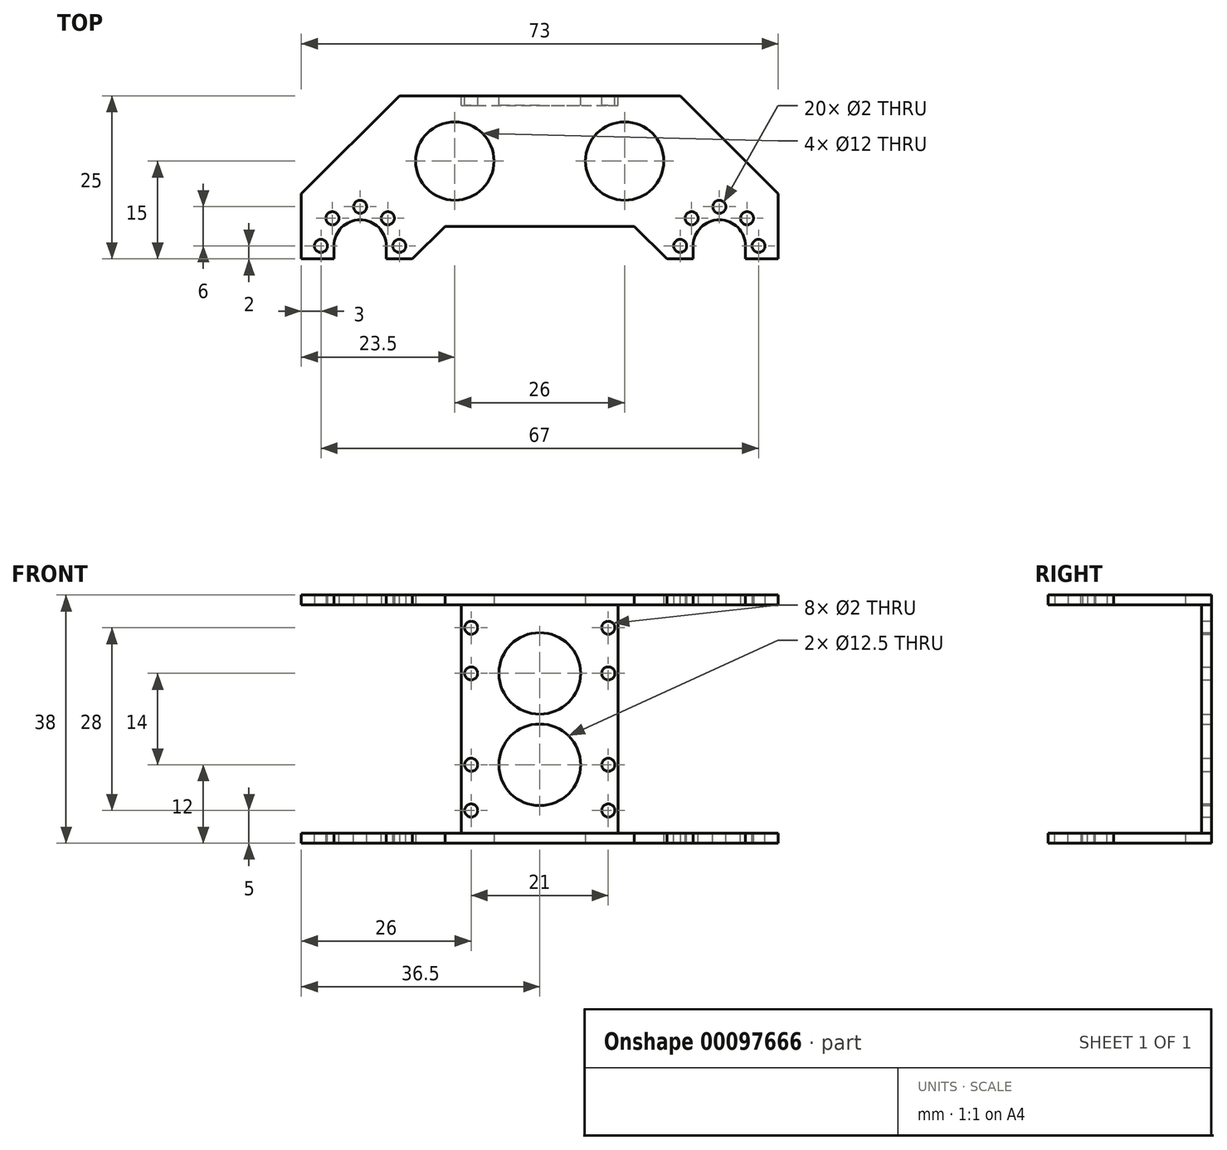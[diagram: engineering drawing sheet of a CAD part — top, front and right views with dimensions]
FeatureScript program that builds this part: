
annotation { "Feature Type Name" : "Feature", "Feature Type Description" : "" }
export const myFeature = defineFeature(function(context is Context, id is Id, definition is map)
    precondition{}
    {
        {
            var Q0;
            Q0=qCreatedBy(makeId("Top.planeOp"),FACE);
            var sketch = newSketch(context, id + "F0", { "sketchPlane" : qUnion([Q0])});
            skLineSegment(sketch, "E0.bottom", {"start": v(-36.5, 0) * mm, "end": v(-31.5, 0) * mm});
            skLineSegment(sketch, "E0.top", {"start": v(-36.5, 25) * mm, "end": v(36.5, 25) * mm});
            skLineSegment(sketch, "E0.left", {"start": v(-36.5, 0) * mm, "end": v(-36.5, 25) * mm});
            skLineSegment(sketch, "E0.right", {"start": v(36.5, 0) * mm, "end": v(36.5, 25) * mm});
            skLineSegment(sketch, "E1", {"start": v(0, 25) * mm, "end": v(0, 0) * mm, "construction": true});
            skArc(sketch, "E2", {"start": v(-23.5, 2) * mm, "mid": v(-27.5, 6) * mm, "end": v(-31.5, 2) * mm});
            skCircle(sketch, "E3", {"center": v(-27.5, 8) * mm, "radius": 1 * mm});
            skCircle(sketch, "E4.1.0", {"center": v(-31.74, 6.24) * mm, "radius": 1 * mm});
            skCircle(sketch, "E4.2.0", {"center": v(-33.5, 2) * mm, "radius": 1 * mm});
            skCircle(sketch, "E4.6.0", {"center": v(-21.5, 2) * mm, "radius": 1 * mm});
            skCircle(sketch, "E4.7.0", {"center": v(-23.26, 6.24) * mm, "radius": 1 * mm});
            skLineSegment(sketch, "E5", {"start": v(-23.5, 2) * mm, "end": v(-23.5, 0) * mm});
            skLineSegment(sketch, "E6", {"start": v(-31.5, 2) * mm, "end": v(-31.5, 0) * mm});
            skLineSegment(sketch, "E7.trimOffspring", {"start": v(-23.5, 0) * mm, "end": v(23.5, 0) * mm});
            skCircle(sketch, "E8.MirrorC", {"center": v(33.5, 2) * mm, "radius": 1 * mm});
            skCircle(sketch, "E9.MirrorC", {"center": v(31.74, 6.24) * mm, "radius": 1 * mm});
            skCircle(sketch, "E10.MirrorC", {"center": v(27.5, 8) * mm, "radius": 1 * mm});
            skCircle(sketch, "E11.MirrorC", {"center": v(23.26, 6.24) * mm, "radius": 1 * mm});
            skCircle(sketch, "E12.MirrorC", {"center": v(21.5, 2) * mm, "radius": 1 * mm});
            skArc(sketch, "E13.MirrorCS", {"start": v(23.5, 2) * mm, "mid": v(27.5, 6) * mm, "end": v(31.5, 2) * mm});
            skLineSegment(sketch, "E14.MirrorCS", {"start": v(23.5, 2) * mm, "end": v(23.5, 0) * mm});
            skLineSegment(sketch, "E15.MirrorCS", {"start": v(31.5, 2) * mm, "end": v(31.5, 0) * mm});
            skLineSegment(sketch, "E16.trimOffspring", {"start": v(31.5, 0) * mm, "end": v(36.5, 0) * mm});
            skSolve(sketch);
        }
        {
            var Q0;
            Q0 = qSketchRegion(id + "F0", true);
            extrude(context, id + "F1", {"entities" : qUnion([Q0]), "depth" : 1.5 * mm});
        }
        {
            var Q0;
            Q0=makeQuery(id+"F1.opExtrude","CAP_FACE",FACE,{"disambiguationData":[OSD([sQuery(id+"F0.wireOp",EDGE,"E0.bottom"),sQuery(id+"F0.wireOp",EDGE,"E0.top"),sQuery(id+"F0.wireOp",EDGE,"E0.left"),sQuery(id+"F0.wireOp",EDGE,"E0.right"),sQuery(id+"F0.wireOp",EDGE,"E2"),sQuery(id+"F0.wireOp",EDGE,"E3"),sQuery(id+"F0.wireOp",EDGE,"E4.1.0"),sQuery(id+"F0.wireOp",EDGE,"E4.2.0"),sQuery(id+"F0.wireOp",EDGE,"E4.6.0"),sQuery(id+"F0.wireOp",EDGE,"E4.7.0"),sQuery(id+"F0.wireOp",EDGE,"E5"),sQuery(id+"F0.wireOp",EDGE,"E6"),sQuery(id+"F0.wireOp",EDGE,"E7.trimOffspring"),sQuery(id+"F0.wireOp",EDGE,"E8.MirrorC"),sQuery(id+"F0.wireOp",EDGE,"E9.MirrorC"),sQuery(id+"F0.wireOp",EDGE,"E10.MirrorC"),sQuery(id+"F0.wireOp",EDGE,"E11.MirrorC"),sQuery(id+"F0.wireOp",EDGE,"E12.MirrorC"),sQuery(id+"F0.wireOp",EDGE,"E13.MirrorCS"),sQuery(id+"F0.wireOp",EDGE,"E14.MirrorCS"),sQuery(id+"F0.wireOp",EDGE,"E15.MirrorCS"),sQuery(id+"F0.wireOp",EDGE,"E16.trimOffspring")])],"isStart":false});
            var sketch = newSketch(context, id + "F2", { "sketchPlane" : qUnion([Q0])});
            skLineSegment(sketch, "E17", {"start": v(-36.5, 10) * mm, "end": v(-21.5, 25) * mm});
            skPoint(sketch, "E18", {"position": v(-27.5, 8) * mm});
            skPoint(sketch, "E19", {"position": v(-21.5, 2) * mm});
            skLineSegment(sketch, "E20", {"start": v(-19.5, 0) * mm, "end": v(-14.5, 5) * mm});
            skLineSegment(sketch, "E21", {"start": v(-14.5, 5) * mm, "end": v(0, 5) * mm});
            skLineSegment(sketch, "E22.MirrorCS", {"start": v(19.5, 0) * mm, "end": v(14.5, 5) * mm});
            skLineSegment(sketch, "E23.MirrorCS", {"start": v(14.5, 5) * mm, "end": v(0, 5) * mm});
            skLineSegment(sketch, "E24.MirrorCS", {"start": v(36.5, 10) * mm, "end": v(21.5, 25) * mm});
            skSolve(sketch);
        }
        {
            var Q0;
            {var subQ0=sQuery(id+"F2.wireOp",EDGE,"E17");Q0=makeQuery(id+"F2.imprint","IMPRINT",FACE,{"disambiguationData":[TD([[makeQuery(id+"F2.imprint","IMPRINT",EDGE,{"derivedFrom":subQ0}),1.0]])]});}
            var Q1;
            {var subQ0=sQuery(id+"F2.wireOp",EDGE,"E24.MirrorCS");Q1=makeQuery(id+"F2.imprint","IMPRINT",FACE,{"disambiguationData":[TD([[makeQuery(id+"F2.imprint","IMPRINT",EDGE,{"derivedFrom":subQ0}),-1.0]])]});}
            var Q2;
            {var subQ1=sQuery(id+"F2.wireOp",EDGE,"E20");Q2=makeQuery(id+"F2.imprint","IMPRINT",FACE,{"disambiguationData":[TD([[makeQuery(id+"F2.imprint","IMPRINT",EDGE,{"derivedFrom":subQ1}),-1.0]])]});}
            extrude(context, id + "F3", {"entities" : qUnion([Q0, Q1, Q2]), "operationType" : NewBodyOperationType.REMOVE, "endBound" : BoundingType.UP_TO_NEXT, "oppositeDirection" : true, "depth" : 25 * mm});
        }
        {
            var Q0;
            Q0=makeQuery(id+"F1.opExtrude","CAP_FACE",FACE,{"disambiguationData":[OSD([sQuery(id+"F0.wireOp",EDGE,"E0.bottom"),sQuery(id+"F0.wireOp",EDGE,"E0.top"),sQuery(id+"F0.wireOp",EDGE,"E0.left"),sQuery(id+"F0.wireOp",EDGE,"E0.right"),sQuery(id+"F0.wireOp",EDGE,"E2"),sQuery(id+"F0.wireOp",EDGE,"E3"),sQuery(id+"F0.wireOp",EDGE,"E4.1.0"),sQuery(id+"F0.wireOp",EDGE,"E4.2.0"),sQuery(id+"F0.wireOp",EDGE,"E4.6.0"),sQuery(id+"F0.wireOp",EDGE,"E4.7.0"),sQuery(id+"F0.wireOp",EDGE,"E5"),sQuery(id+"F0.wireOp",EDGE,"E6"),sQuery(id+"F0.wireOp",EDGE,"E7.trimOffspring"),sQuery(id+"F0.wireOp",EDGE,"E8.MirrorC"),sQuery(id+"F0.wireOp",EDGE,"E9.MirrorC"),sQuery(id+"F0.wireOp",EDGE,"E10.MirrorC"),sQuery(id+"F0.wireOp",EDGE,"E11.MirrorC"),sQuery(id+"F0.wireOp",EDGE,"E12.MirrorC"),sQuery(id+"F0.wireOp",EDGE,"E13.MirrorCS"),sQuery(id+"F0.wireOp",EDGE,"E14.MirrorCS"),sQuery(id+"F0.wireOp",EDGE,"E15.MirrorCS"),sQuery(id+"F0.wireOp",EDGE,"E16.trimOffspring")])],"isStart":true});
            var sketch = newSketch(context, id + "F4", { "sketchPlane" : qUnion([Q0])});
            skLineSegment(sketch, "E25.bottom", {"start": v(-21.5, -25) * mm, "end": v(21.5, -25) * mm});
            skLineSegment(sketch, "E25.top", {"start": v(-21.5, -23.5) * mm, "end": v(21.5, -23.5) * mm});
            skLineSegment(sketch, "E25.left", {"start": v(-21.5, -25) * mm, "end": v(-21.5, -23.5) * mm});
            skLineSegment(sketch, "E25.right", {"start": v(21.5, -25) * mm, "end": v(21.5, -23.5) * mm});
            skPoint(sketch, "E25.middle", {"position": v(0, -24.25) * mm});
            skLineSegment(sketch, "E26", {"start": v(12, -23.5) * mm, "end": v(12, -25) * mm});
            skLineSegment(sketch, "E27.MirrorCS", {"start": v(-12, -23.5) * mm, "end": v(-12, -25) * mm});
            skSolve(sketch);
        }
        {
            var Q0;
            {var subQ0=sQuery(id+"F4.wireOp",EDGE,"E26");Q0=makeQuery(id+"F4.imprint","IMPRINT",FACE,{"disambiguationData":[TD([[makeQuery(id+"F4.imprint","IMPRINT",EDGE,{"derivedFrom":subQ0}),-1.0]])]});}
            extrude(context, id + "F5", {"entities" : qUnion([Q0]), "operationType" : NewBodyOperationType.ADD, "depth" : (35 / 2) * mm});
        }
        {
            var Q0;
            Q0=qCreatedBy(makeId("Top.planeOp"),FACE);
            cPlane(context, id + "F6", {"entities" : qUnion([Q0]), "cplaneType" : CPlaneType.OFFSET, "offset" : (35 / 2) * mm, "oppositeDirection" : true, "width" : 150 * mm, "height" : 150 * mm});
        }
        {
            var Q0;
            Q0=makeQuery(id+"F1.opExtrude","SWEPT_BODY",BODY,{"disambiguationData":[OSD([sQuery(id+"F0.wireOp",EDGE,"E0.bottom"),sQuery(id+"F0.wireOp",EDGE,"E0.top"),sQuery(id+"F0.wireOp",EDGE,"E0.left"),sQuery(id+"F0.wireOp",EDGE,"E0.right"),sQuery(id+"F0.wireOp",EDGE,"E2"),sQuery(id+"F0.wireOp",EDGE,"E3"),sQuery(id+"F0.wireOp",EDGE,"E4.1.0"),sQuery(id+"F0.wireOp",EDGE,"E4.2.0"),sQuery(id+"F0.wireOp",EDGE,"E4.6.0"),sQuery(id+"F0.wireOp",EDGE,"E4.7.0"),sQuery(id+"F0.wireOp",EDGE,"E5"),sQuery(id+"F0.wireOp",EDGE,"E6"),sQuery(id+"F0.wireOp",EDGE,"E7.trimOffspring"),sQuery(id+"F0.wireOp",EDGE,"E8.MirrorC"),sQuery(id+"F0.wireOp",EDGE,"E9.MirrorC"),sQuery(id+"F0.wireOp",EDGE,"E10.MirrorC"),sQuery(id+"F0.wireOp",EDGE,"E11.MirrorC"),sQuery(id+"F0.wireOp",EDGE,"E12.MirrorC"),sQuery(id+"F0.wireOp",EDGE,"E13.MirrorCS"),sQuery(id+"F0.wireOp",EDGE,"E14.MirrorCS"),sQuery(id+"F0.wireOp",EDGE,"E15.MirrorCS"),sQuery(id+"F0.wireOp",EDGE,"E16.trimOffspring")])]});
            var Q1;
            Q1=qCreatedBy(id+"F6.planeOp",FACE);
            mirror(context, id + "F7", {"operationType" : NewBodyOperationType.ADD, "entities" : qUnion([Q0]), "mirrorPlane" : qUnion([Q1])});
        }
        {
            var Q0;
            Q0=makeQuery(id+"F7.opPattern","COPY",FACE,{"derivedFrom":makeQuery(id+"F1.opExtrude","CAP_FACE",FACE,{"disambiguationData":[OSD([sQuery(id+"F0.wireOp",EDGE,"E0.bottom"),sQuery(id+"F0.wireOp",EDGE,"E0.top"),sQuery(id+"F0.wireOp",EDGE,"E0.left"),sQuery(id+"F0.wireOp",EDGE,"E0.right"),sQuery(id+"F0.wireOp",EDGE,"E2"),sQuery(id+"F0.wireOp",EDGE,"E3"),sQuery(id+"F0.wireOp",EDGE,"E4.1.0"),sQuery(id+"F0.wireOp",EDGE,"E4.2.0"),sQuery(id+"F0.wireOp",EDGE,"E4.6.0"),sQuery(id+"F0.wireOp",EDGE,"E4.7.0"),sQuery(id+"F0.wireOp",EDGE,"E5"),sQuery(id+"F0.wireOp",EDGE,"E6"),sQuery(id+"F0.wireOp",EDGE,"E7.trimOffspring"),sQuery(id+"F0.wireOp",EDGE,"E8.MirrorC"),sQuery(id+"F0.wireOp",EDGE,"E9.MirrorC"),sQuery(id+"F0.wireOp",EDGE,"E10.MirrorC"),sQuery(id+"F0.wireOp",EDGE,"E11.MirrorC"),sQuery(id+"F0.wireOp",EDGE,"E12.MirrorC"),sQuery(id+"F0.wireOp",EDGE,"E13.MirrorCS"),sQuery(id+"F0.wireOp",EDGE,"E14.MirrorCS"),sQuery(id+"F0.wireOp",EDGE,"E15.MirrorCS"),sQuery(id+"F0.wireOp",EDGE,"E16.trimOffspring")])],"isStart":false}),"instanceName":"1"});
            var sketch = newSketch(context, id + "F8", { "sketchPlane" : qUnion([Q0])});
            skCircle(sketch, "E28", {"center": v(-13, -15) * mm, "radius": 6 * mm});
            skCircle(sketch, "E29.MirrorC", {"center": v(13, -15) * mm, "radius": 6 * mm});
            skSolve(sketch);
        }
        {
            var Q0;
            Q0 = qSketchRegion(id + "F8", true);
            extrude(context, id + "F9", {"entities" : qUnion([Q0]), "operationType" : NewBodyOperationType.REMOVE, "endBound" : BoundingType.THROUGH_ALL, "oppositeDirection" : true, "depth" : 25 * mm});
        }
        {
            var Q0;
            {var subQ0=makeQuery(id+"F5.boolean.opBoolean","MERGE",FACE,{"derivedFrom":[makeQuery(id+"F1.opExtrude","SWEPT_FACE",FACE,{"disambiguationData":[OSD([sQuery(id+"F0.wireOp",EDGE,"E0.top")])]}),makeQuery(id+"F5.opExtrude","SWEPT_FACE",FACE,{"disambiguationData":[OSD([sQuery(id+"F4.wireOp",EDGE,"E25.bottom")])]})]});Q0=makeQuery(id+"F7.boolean.opBoolean","MERGE",FACE,{"derivedFrom":[subQ0,makeQuery(id+"F7.opPattern","COPY",FACE,{"derivedFrom":subQ0,"instanceName":"1"})]});}
            var sketch = newSketch(context, id + "F10", { "sketchPlane" : qUnion([Q0])});
            skCircle(sketch, "E30", {"center": v(10.5, -10.5) * mm, "radius": 1 * mm});
            skCircle(sketch, "E31", {"center": v(10.5, -31.5) * mm, "radius": 1 * mm});
            skCircle(sketch, "E32.MirrorC", {"center": v(-10.5, -10.5) * mm, "radius": 1 * mm});
            skCircle(sketch, "E33.MirrorC", {"center": v(-10.5, -31.5) * mm, "radius": 1 * mm});
            skCircle(sketch, "E34", {"center": v(0, -10.5) * mm, "radius": 6.25 * mm});
            skCircle(sketch, "E35.MirrorC", {"center": v(-10.5, -24.5) * mm, "radius": 1 * mm});
            skCircle(sketch, "E36.MirrorC", {"center": v(-10.5, -3.5) * mm, "radius": 1 * mm});
            skCircle(sketch, "E37.MirrorC", {"center": v(10.5, -3.5) * mm, "radius": 1 * mm});
            skCircle(sketch, "E38.MirrorC", {"center": v(10.5, -24.5) * mm, "radius": 1 * mm});
            skCircle(sketch, "E39.MirrorC", {"center": v(0, -24.5) * mm, "radius": 6.25 * mm});
            skSolve(sketch);
        }
        {
            var Q0;
            Q0 = qSketchRegion(id + "F10", true);
            extrude(context, id + "F11", {"entities" : qUnion([Q0]), "operationType" : NewBodyOperationType.REMOVE, "endBound" : BoundingType.UP_TO_NEXT, "oppositeDirection" : true, "depth" : 25 * mm});
        }
    });
